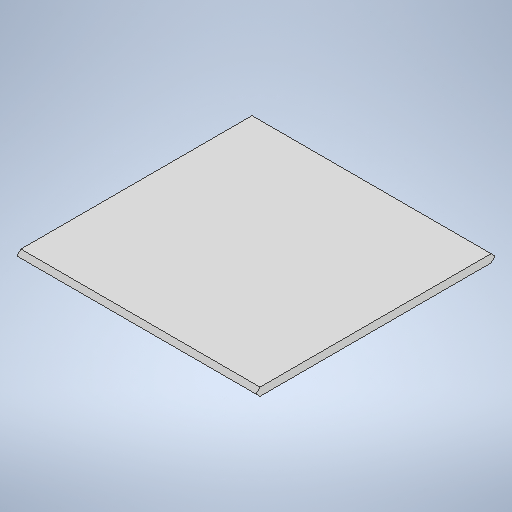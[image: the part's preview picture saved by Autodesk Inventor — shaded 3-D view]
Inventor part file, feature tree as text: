
AUTODESK INVENTOR PART (.ipt)
format: ipt  version: 2025 (Build 290162000, 162)  size: 223,232 bytes
history: native  units: mm
features: extrude x2, sketch x2
ambient origin geometry x8: Origin, YZ Plane, XZ Plane, XY Plane, X Axis, Y Axis, Z Axis, Center Point
bodies: Solid1 (feature_tree)
feature tree (4):
  extrude  "Extrusion1"  Depth=44.8mm
  extrude  "Extrusion2"  TaperAngle=45.0deg  [1 undecoded]
  sketch  "Sketch1"  dims[d0=44.8mm d1=44.8mm]
  sketch  "Sketch2"  dims[d2=1.5mm d3=0.0mm d7=45.0deg d8=45.0deg d9=0.0mm d10=0.0mm]
note: 1 required parameter value undecoded (feature->parameter linkage not recoverable at this tier; creation-order binding heuristic only, values carry confidence <= 0.55)
